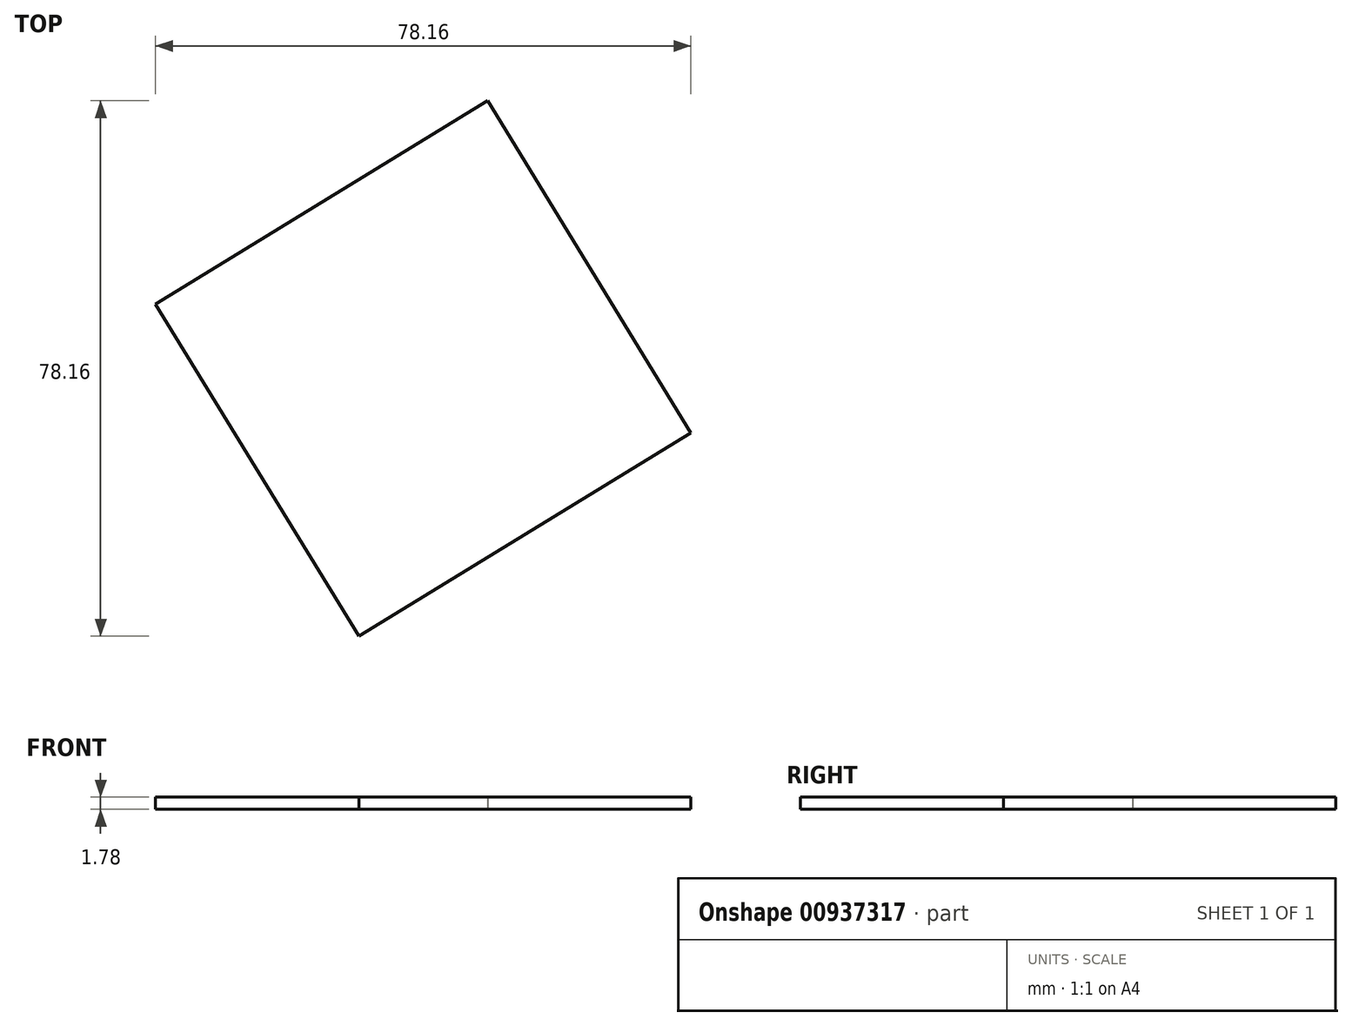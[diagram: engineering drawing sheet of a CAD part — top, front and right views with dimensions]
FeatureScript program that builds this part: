
annotation { "Feature Type Name" : "Feature", "Feature Type Description" : "" }
export const myFeature = defineFeature(function(context is Context, id is Id, definition is map)
    precondition{}
    {
        {
            var Q0;
            Q0=qCreatedBy(makeId("Top.planeOp"),FACE);
            var sketch = newSketch(context, id + "F0", { "sketchPlane" : qUnion([Q0])});
            skCircle(sketch, "E0.cCircle", {"center": v(-23.53, 31.1) * mm, "radius": 28.42 * mm, "construction": true});
            skLineSegment(sketch, "E0.0", {"start": v(15.55, 21.68) * mm, "end": v(-32.95, -7.99) * mm});
            skLineSegment(sketch, "E0.1", {"start": v(-32.95, -7.99) * mm, "end": v(-62.61, 40.5) * mm});
            skLineSegment(sketch, "E0.2", {"start": v(-62.61, 40.5) * mm, "end": v(-14.12, 70.17) * mm});
            skLineSegment(sketch, "E0.3", {"start": v(-14.12, 70.17) * mm, "end": v(15.55, 21.68) * mm});
            skPoint(sketch, "E0.0.midPoint", {"position": v(-8.7, 6.85) * mm});
            skSolve(sketch);
        }
        {
            var Q0;
            Q0=makeQuery(id+"F0.imprint","IMPRINT",FACE,{"disambiguationData":[TD([[makeQuery(id+"F0.imprint","IMPRINT",EDGE,{"derivedFrom":sQuery(id+"F0.wireOp",EDGE,"E0.0")}),-1.0]])]});
            extrude(context, id + "F1", {"entities" : qUnion([Q0]), "depth" : 1.78 * mm, "offsetDistance" : 25.4 * mm});
        }
    });
